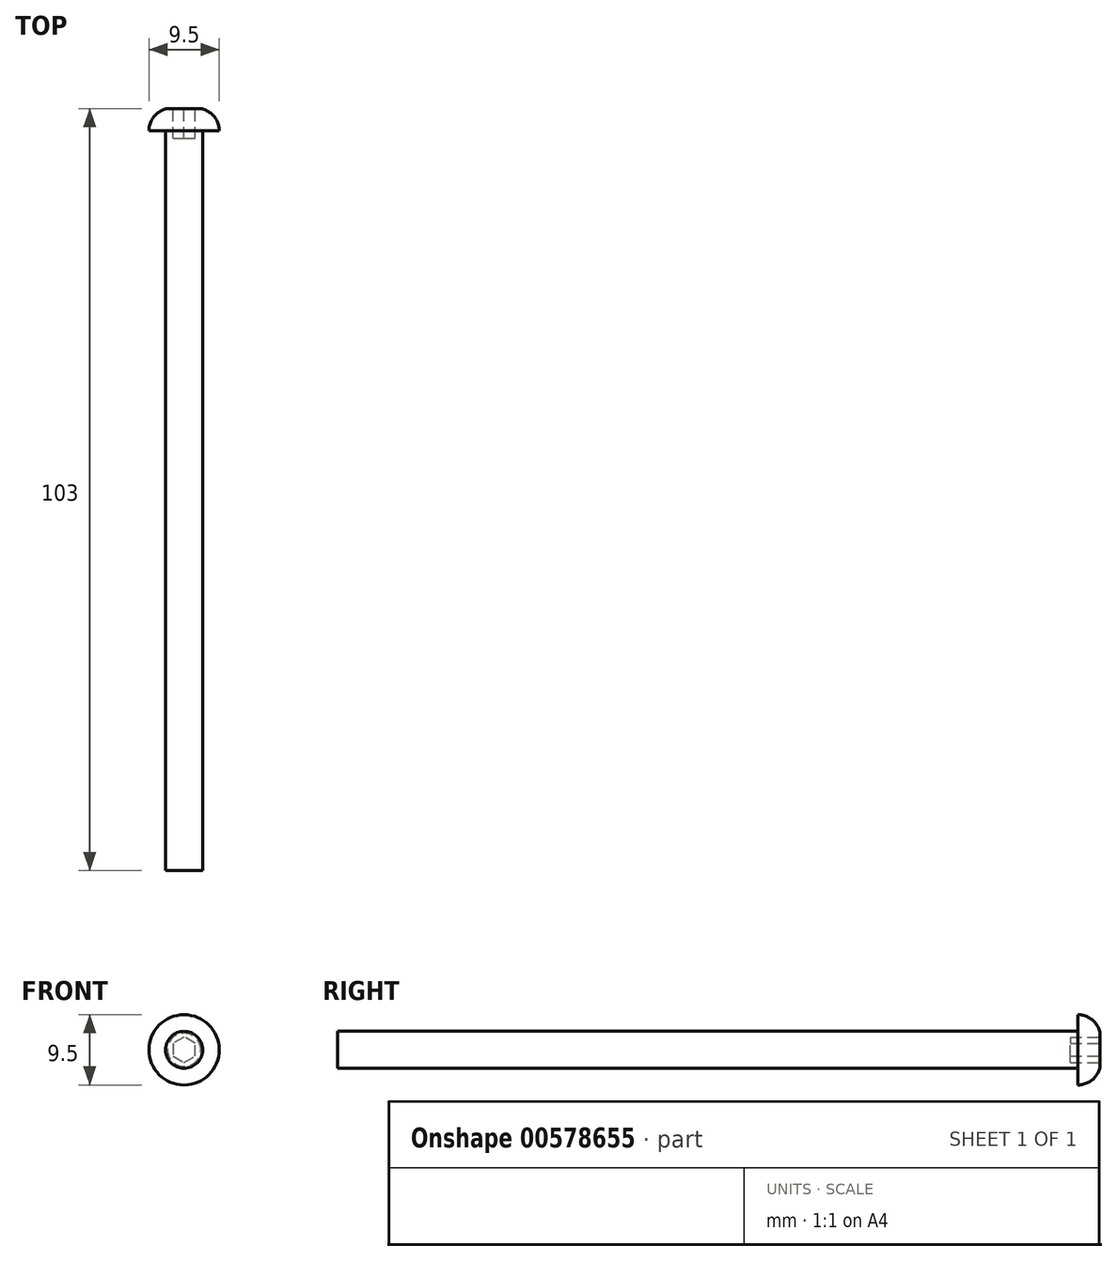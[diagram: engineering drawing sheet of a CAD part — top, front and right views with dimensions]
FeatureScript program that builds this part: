
annotation { "Feature Type Name" : "Feature", "Feature Type Description" : "" }
export const myFeature = defineFeature(function(context is Context, id is Id, definition is map)
    precondition{}
    {
        {
            var Q0;
            Q0=qCreatedBy(makeId("Front.planeOp"),FACE);
            var sketch = newSketch(context, id + "F0", { "sketchPlane" : qUnion([Q0])});
            skCircle(sketch, "E0", {"center": v(0, 0) * mm, "radius": 2.5 * mm});
            skSolve(sketch);
        }
        {
            var Q0;
            Q0=qSketchRegion(id+"F0",true);
            extrude(context, id + "F1", {"entities" : qUnion([Q0]), "depth" : 100 * mm, "offsetDistance" : 25 * mm});
        }
        {
            var Q0;
            Q0=qCreatedBy(makeId("Right.planeOp"),FACE);
            var sketch = newSketch(context, id + "F2", { "sketchPlane" : qUnion([Q0])});
            skLineSegment(sketch, "E1", {"start": v(0, 0) * mm, "end": v(0, 4.75) * mm});
            skLineSegment(sketch, "E2", {"start": v(0, 0) * mm, "end": v(3, 0) * mm});
            skLineSegment(sketch, "E3", {"start": v(3, 0) * mm, "end": v(3, 1.5) * mm});
            skLineSegment(sketch, "E4", {"start": v(3, 1.5) * mm, "end": v(3, 2.25) * mm});
            skArc(sketch, "E5", {"start": v(3, 2.25) * mm, "mid": v(1.95, 4.04) * mm, "end": v(0, 4.75) * mm});
            skSolve(sketch);
        }
        {
            var Q0;
            Q0=qSketchRegion(id+"F2",true);
            var Q1;
            Q1=makeQuery(id+"F1.opExtrude","CAP_EDGE",EDGE,{"disambiguationData":[OSD([sQuery(id+"F0.wireOp",EDGE,"E0")])],"isStart":true});
            revolve(context, id + "F3", {"operationType" : NewBodyOperationType.ADD, "entities" : qUnion([Q0]), "axis" : qUnion([Q1]), "revolveType" : RevolveType.FULL});
        }
        {
            var Q0;
            Q0=makeQuery(id+"F3.opRevolve","SWEPT_FACE",FACE,{"disambiguationData":[OSD([sQuery(id+"F2.wireOp",EDGE,"E3"),sQuery(id+"F2.wireOp",EDGE,"E4")])]});
            var sketch = newSketch(context, id + "F4", { "sketchPlane" : qUnion([Q0])});
            skCircle(sketch, "E6.cCircle", {"center": v(0, 0) * mm, "radius": 1.5 * mm, "construction": true});
            skLineSegment(sketch, "E6.0", {"start": v(-1.5, -0.87) * mm, "end": v(-1.5, 0.87) * mm});
            skLineSegment(sketch, "E6.1", {"start": v(-1.5, 0.87) * mm, "end": v(0, 1.73) * mm});
            skLineSegment(sketch, "E6.2", {"start": v(0, 1.73) * mm, "end": v(1.5, 0.87) * mm});
            skLineSegment(sketch, "E6.3", {"start": v(1.5, 0.87) * mm, "end": v(1.5, -0.87) * mm});
            skLineSegment(sketch, "E6.4", {"start": v(1.5, -0.87) * mm, "end": v(0, -1.73) * mm});
            skLineSegment(sketch, "E6.5", {"start": v(0, -1.73) * mm, "end": v(-1.5, -0.87) * mm});
            skPoint(sketch, "E6.0.midPoint", {"position": v(-1.5, 0) * mm});
            skSolve(sketch);
        }
        {
            var Q0;
            Q0=qSketchRegion(id+"F4",true);
            extrude(context, id + "F5", {"entities" : qUnion([Q0]), "operationType" : NewBodyOperationType.REMOVE, "oppositeDirection" : true, "depth" : 4 * mm, "offsetDistance" : 25 * mm});
        }
    });
